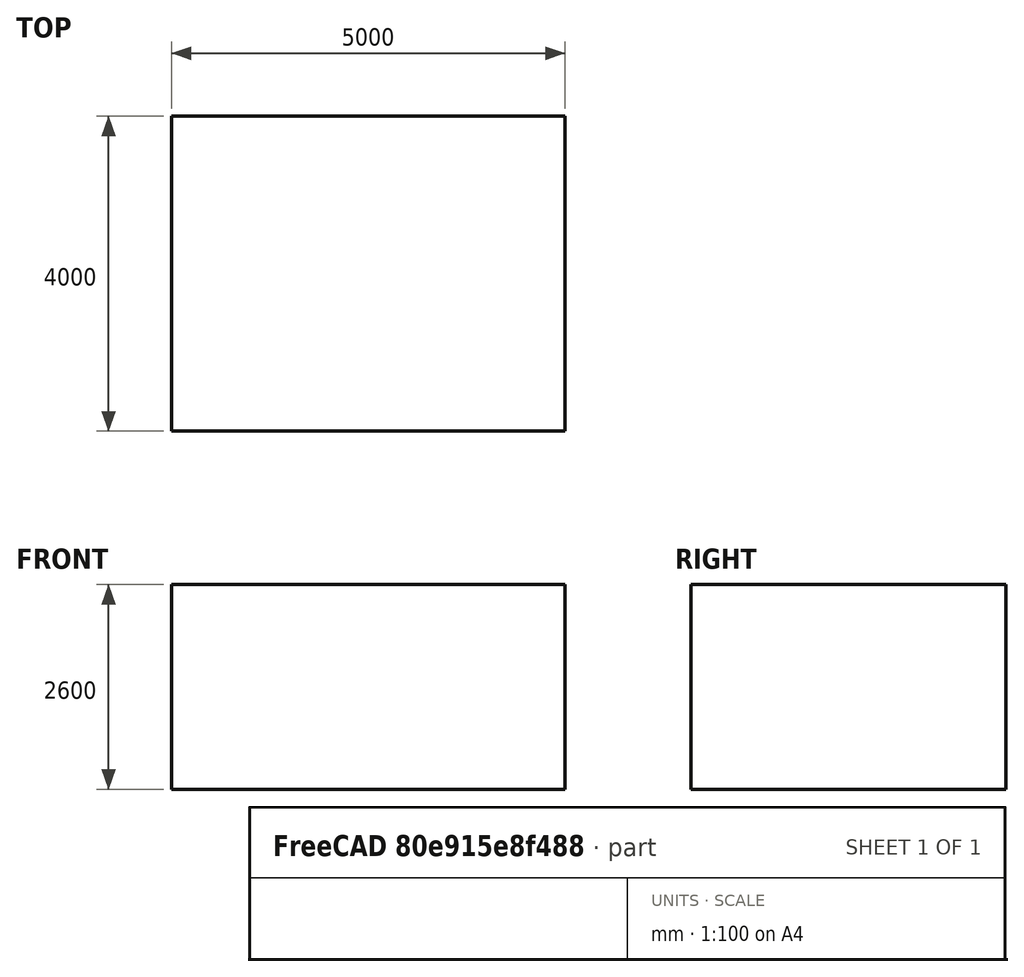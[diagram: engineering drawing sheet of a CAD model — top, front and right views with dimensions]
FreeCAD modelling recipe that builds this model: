
FCSTD DOCUMENT  (FreeCAD 0.19R24291 (Git))
Label: sala5x6x2
License: All rights reserved
LicenseURL: http://en.wikipedia.org/wiki/All_rights_reserved
objects: Sketcher::SketchObject×1, PartDesign::Pad×1, PartDesign::Body×1
note: 4 computed .brp shape members not serialized (recipe doc carries the construction recipe); baked Part::Feature solids carry a one-line shape summary decoded from their .brp

FEATURE [Sketcher::SketchObject] Sketch
  FullyConstrained = true
  MapMode = 5
  Support = -> [XY_Plane]
  sketch-geometry (4):
    g0: LineSegment StartX=0 StartY=4000 StartZ=0 EndX=5000 EndY=4000 EndZ=0
    g1: LineSegment StartX=5000 StartY=4000 StartZ=0 EndX=5000 EndY=0 EndZ=0
    g2: LineSegment StartX=5000 StartY=0 StartZ=0 EndX=0 EndY=0 EndZ=0
    g3: LineSegment StartX=0 StartY=0 StartZ=0 EndX=0 EndY=4000 EndZ=0
  constraints (11):
    c: Coincident(g0,g1)
    c: Coincident(g1,g2)
    c: Coincident(g2,g3)
    c: Coincident(g3,g0)
    c: Horizontal(g0)
    c: Horizontal(g2)
    c: Vertical(g1)
    c: Vertical(g3)
    c: DistanceX(g0,g0) = 5000
    c: DistanceY(g1,g1) = 4000
    c: Coincident(g2,g-1)
FEATURE [PartDesign::Pad] Pad
  Direction = (1,1,1)
  Length = 2600
  Length2 = 100
  Profile = -> Sketch
  Type = 0
FEATURE [PartDesign::Body] Body
  Group = -> [Sketch,Pad]
  Origin = -> Origin
  Tip = -> Pad
